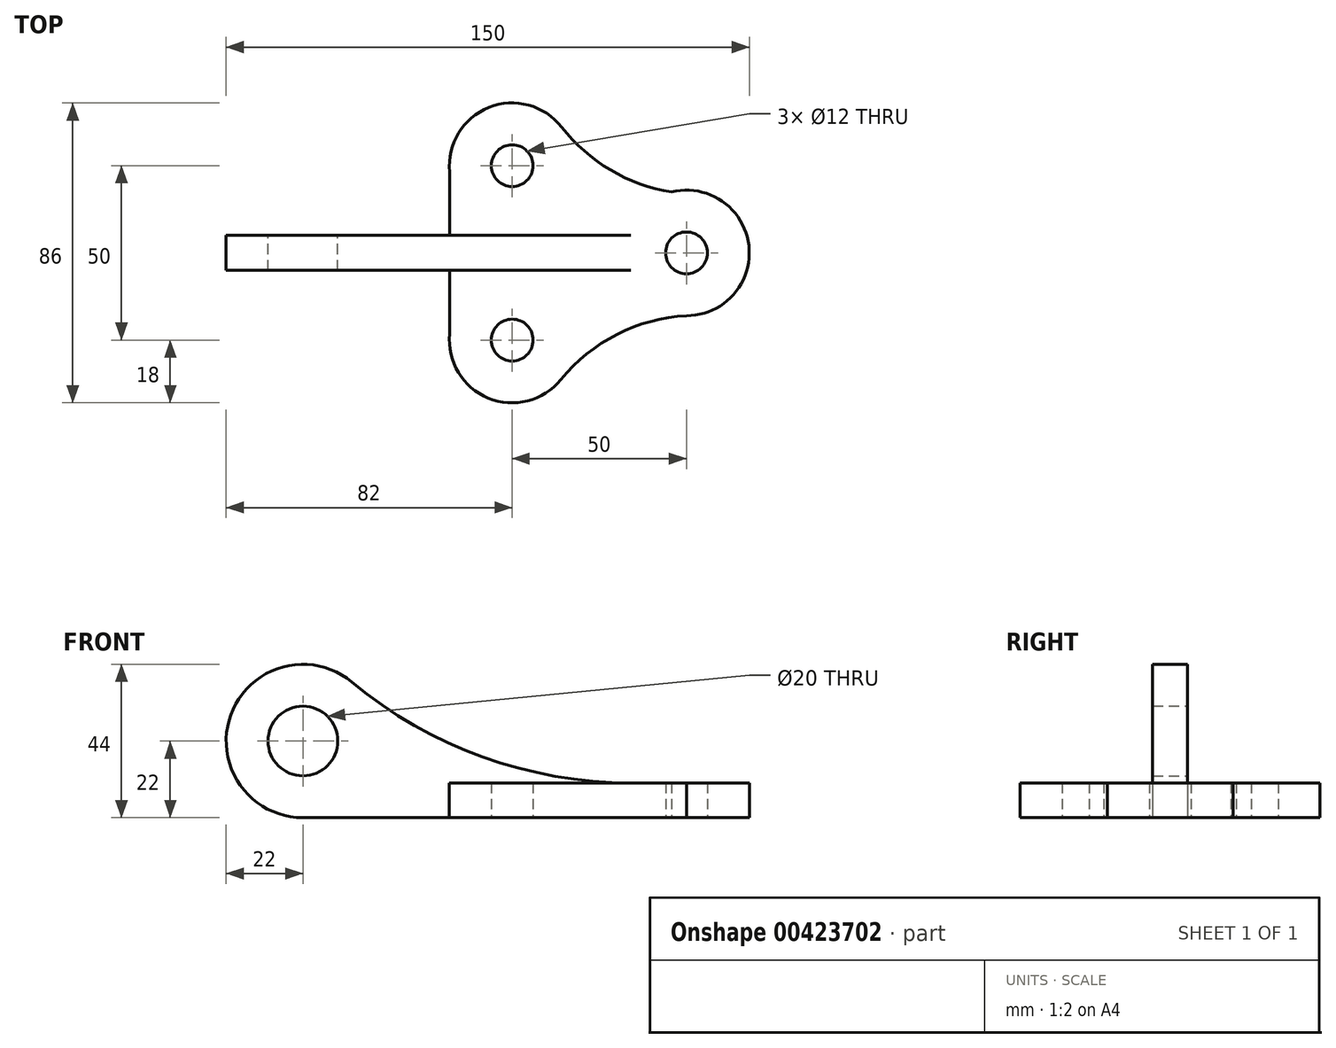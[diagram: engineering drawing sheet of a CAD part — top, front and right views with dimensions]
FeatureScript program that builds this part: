
annotation { "Feature Type Name" : "Feature", "Feature Type Description" : "" }
export const myFeature = defineFeature(function(context is Context, id is Id, definition is map)
    precondition{}
    {
        {
            var Q0;
            Q0=qCreatedBy(makeId("Top.planeOp"),FACE);
            var sketch = newSketch(context, id + "F0", { "sketchPlane" : qUnion([Q0])});
            skArc(sketch, "E0", {"start": v(-35.81, 36.08) * mm, "mid": v(-56.68, 41.71) * mm, "end": v(-67.91, 23.25) * mm});
            skCircle(sketch, "E1", {"center": v(-50, 25) * mm, "radius": 6 * mm});
            skArc(sketch, "E2", {"start": v(-67.91, -23.25) * mm, "mid": v(-56.85, -41.65) * mm, "end": v(-36.04, -36.36) * mm});
            skCircle(sketch, "E3", {"center": v(-50, -25) * mm, "radius": 6 * mm});
            skArc(sketch, "E4", {"start": v(0, -18) * mm, "mid": v(17.87, 2.16) * mm, "end": v(-4.28, 17.48) * mm});
            skCircle(sketch, "E5", {"center": v(0, 0) * mm, "radius": 6 * mm});
            skArc(sketch, "E6", {"start": v(-35.81, 36.08) * mm, "mid": v(-17.18, 21.38) * mm, "end": v(6.13, 16.92) * mm});
            skArc(sketch, "E7", {"start": v(0, -18) * mm, "mid": v(-19.96, -23.37) * mm, "end": v(-36.04, -36.36) * mm});
            skLineSegment(sketch, "E8", {"start": v(-67.91, 26.75) * mm, "end": v(-67.91, -26.75) * mm});
            skSolve(sketch);
        }
        {
            var Q0;
            Q0 = qSketchRegion(id + "F0", true);
            extrude(context, id + "F1", {"entities" : qUnion([Q0]), "depth" : 10 * mm});
        }
        {
            var Q0;
            Q0=qCreatedBy(makeId("Front.planeOp"),FACE);
            var sketch = newSketch(context, id + "F2", { "sketchPlane" : qUnion([Q0])});
            skLineSegment(sketch, "E9", {"start": v(18, 10) * mm, "end": v(18, 0) * mm});
            skLineSegment(sketch, "E10", {"start": v(-46.43, 0) * mm, "end": v(-110, 0) * mm});
            skArc(sketch, "E11", {"start": v(-95.93, 38.91) * mm, "mid": v(-130.69, 29.48) * mm, "end": v(-110, 0) * mm});
            skCircle(sketch, "E12", {"center": v(-110, 22) * mm, "radius": 10 * mm});
            skArc(sketch, "E13", {"start": v(-95.93, 38.91) * mm, "mid": v(-58.49, 17.45) * mm, "end": v(-15.98, 10) * mm});
            skPoint(sketch, "E14.0.end.orphan", {"position": v(6, 10) * mm});
            skPoint(sketch, "E14.0.start.orphan", {"position": v(-6, 10) * mm});
            skLineSegment(sketch, "E15.trimOffspring", {"start": v(-6, 10) * mm, "end": v(-15.98, 10) * mm});
            skLineSegment(sketch, "E16", {"start": v(-46.43, 0) * mm, "end": v(-9.93, 0) * mm});
            skLineSegment(sketch, "E17", {"start": v(-15.98, 10) * mm, "end": v(-6, 10) * mm});
            skLineSegment(sketch, "E18", {"start": v(-15.98, 10) * mm, "end": v(-9.93, 0) * mm});
            skSolve(sketch);
        }
        {
            var Q0;
            Q0 = qSketchRegion(id + "F2", true);
            extrude(context, id + "F3", {"entities" : qUnion([Q0]), "operationType" : NewBodyOperationType.ADD, "depth" : 5 * mm, "hasSecondDirection" : true, "secondDirectionOppositeDirection" : true, "secondDirectionDepth" : 5 * mm});
        }
    });
